# Revit family: Electronics_Visual-TVs_ViewSonic_The-ViewSonicR-CDX5562-Commercial-Displa
name_source: partatom
category: Electrical Equipment
revit_build: Autodesk Revit 2015 (Build: 20140606_1530(x64)
units: mm (PartAtom-declared; Revit-internal decimal feet)

## types (1)
- CDX5562
    Assembly Code = D50
    BIMobject category = Visual - TVs
    BIMobject category code = electronics-visual-tvs
    BIMobject main category = Electronics
    BIMobject main category code = electronics
    BOSUseNativeGeometries = 1
    Brand url = https://www.viewsonic.com
    Covering Color = Plastic - Viewsonic - Black
    Description = The ViewSonic® CDX5562 is a 55" (54.64’’ viewable) commercial display with a super ultra-narrow bezel optimized for multi-panel video wall applications. With an edge-to-edge bezel width of only 1.8mm between combined displays, and 10x10 installation via DisplayPort or DVI daisy-chain, the CDX5562 delivers nearly seamless, high-impact video walls for public, retail, and transportation settings. With Full HD 1080p resolution, 700-nit high brightness, SuperClear® technology for wide viewing angles, and dual 10W stereo speakers, the CDX5562 delivers sharp, vivid images with incredible sound and multimedia performance.
    Design country = Taiwan
    Edition number = 1
    Keynote = V90
    Manufacturer = ViewSonic
    Manufacturer country = Taiwan
    Manufacturer name = ViewSonic
    Model = viewsonic_cdx5562
    Product Guid = ecd0aff0-4434-4a1a-9642-d6315b357b76
    Product SKU = viewsonic_cdx5562
    Product data url = https://bimobject.com
    Product family = Electronics
    Product group = Commercial Displays
    Product name = The ViewSonic® CDX5562 Commercial Display
    Product url = https://www.viewsonic.com
    QR code = http://bimobject.com
    URL = www.viewsonic.com

## geometry (parser evidence)
native form markers: Sweep x3
no freeform markers — native parametric forms only
